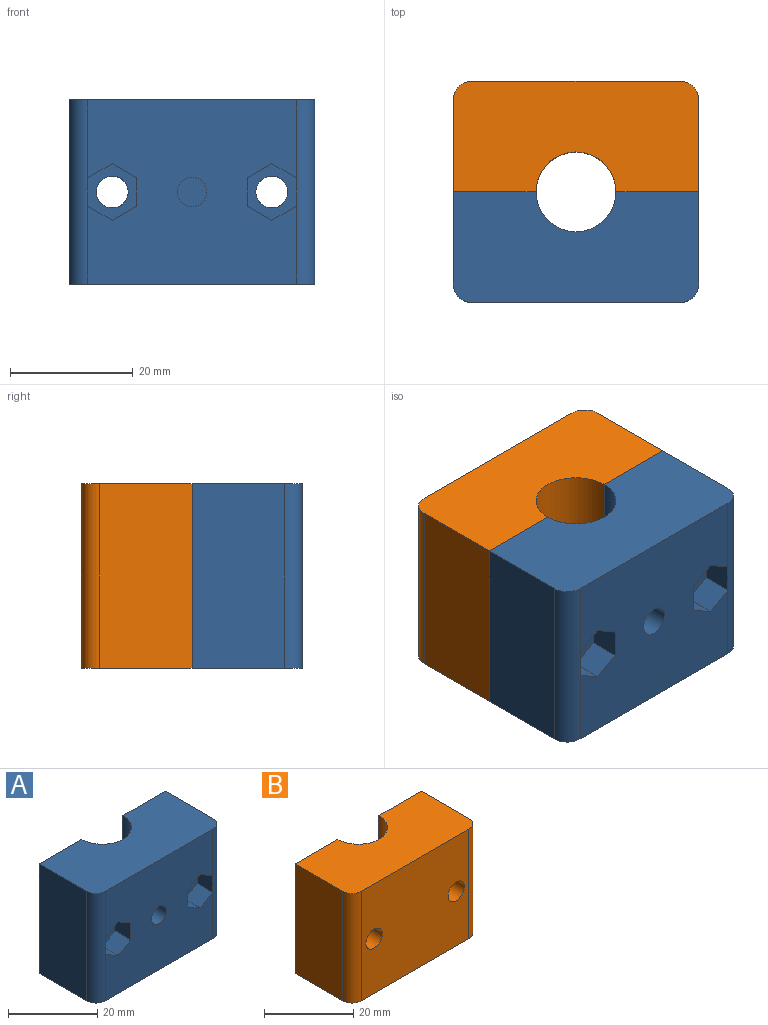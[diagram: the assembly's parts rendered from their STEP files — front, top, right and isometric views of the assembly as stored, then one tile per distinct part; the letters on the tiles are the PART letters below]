
ASSEMBLY  parts=2 mates=1
PART A: 28 faces, bbox 40x18x30 mm
  f0: plane 34x30mm, normal (0,-1,0), area 891.1mm2, adj f5,f6,f10,f11,f12,f14,f15,f17
  f1: cylinder r=2.6mm len=13mm, axis (0,-1,0), area 212.4mm2, adj f8,f27
  f2: cylinder r=2.6mm len=13mm, axis (0,-1,0), area 212.4mm2, adj f3,f20
  f3: plane 30x13.5mm, normal (0,1,0), area 383.8mm2, adj f2,f4,f9,f10,f11
  f4: plane 30x15mm, normal (-1,0,0), area 450mm2, adj f3,f5,f10,f11
  f5: cylinder r=3mm len=30mm, axis (0,0,-1), area 141.4mm2, adj f0,f4,f10,f11,f16
  f6: cylinder r=3mm len=30mm, axis (0,0,-1), area 141.4mm2, adj f0,f7,f10,f11,f26
  f7: plane 30x15mm, normal (1,0,0), area 450mm2, adj f6,f8,f10,f11
  f8: plane 30x13.5mm, normal (0,1,0), area 383.8mm2, adj f1,f7,f9,f10,f11
  f9: cylinder r=6.5mm len=30mm, axis (0,0,-1), area 612.6mm2, adj f3,f8,f10,f11
  f10: plane 40x18mm, normal (0,0,1), area 649.8mm2, adj f0,f3,f4,f5,f6,f7,f8,f9
  f11: plane 40x18mm, normal (0,0,-1), area 649.8mm2, adj f0,f3,f4,f5,f6,f7,f8,f9
  f12: cylinder r=2.4mm len=9mm, axis (0,-1,0), area 135.7mm2, adj f0,f13
  f13: plane 4.8x4.8mm, normal (0,-1,0), area 18.1mm2, adj f12
  f14: plane 5x4mm, normal (-0.5,0,-0.87), area 23.1mm2, adj f0,f15,f19,f20
  f15: plane 5x4mm, normal (0.5,0,-0.87), area 23.1mm2, adj f0,f14,f16,f20
  f16: plane 5x4.62mm, normal (1,0,0), area 23.1mm2, adj f5,f15,f17,f20
  f17: plane 5x4mm, normal (0.5,0,0.87), area 23.1mm2, adj f0,f16,f18,f20
  f18: plane 5x4mm, normal (-0.5,0,0.87), area 23.1mm2, adj f0,f17,f19,f20
  f19: plane 5x4.62mm, normal (-1,0,0), area 23.1mm2, adj f0,f14,f18,f20
  f20: plane 9.24x8mm, normal (0,-1,0), area 34.2mm2, adj f2,f14,f15,f16,f17,f18,f19
  f21: plane 5x4mm, normal (-0.5,0,-0.87), area 23.1mm2, adj f0,f22,f26,f27
  f22: plane 5x4mm, normal (0.5,0,-0.87), area 23.1mm2, adj f0,f21,f23,f27
  f23: plane 5x4.62mm, normal (1,0,0), area 23.1mm2, adj f0,f22,f24,f27
  f24: plane 5x4mm, normal (0.5,0,0.87), area 23.1mm2, adj f0,f23,f25,f27
  f25: plane 5x4mm, normal (-0.5,0,0.87), area 23.1mm2, adj f0,f24,f26,f27
  f26: plane 5x4.62mm, normal (-1,0,0), area 23.1mm2, adj f6,f21,f25,f27
  f27: plane 9.24x8mm, normal (0,-1,0), area 34.2mm2, adj f1,f21,f22,f23,f24,f25,f26
PART B: 12 faces, bbox 40x18x30 mm
  f0: plane 34x30mm, normal (0,-1,0), area 977.5mm2, adj f3,f4,f8,f9,f10,f11
  f1: plane 30x13.5mm, normal (0,1,0), area 383.8mm2, adj f2,f7,f8,f9,f11
  f2: plane 30x15mm, normal (-1,0,0), area 450mm2, adj f1,f3,f8,f9
  f3: cylinder r=3mm len=30mm, axis (0,0,-1), area 141.4mm2, adj f0,f2,f8,f9
  f4: cylinder r=3mm len=30mm, axis (0,0,-1), area 141.4mm2, adj f0,f5,f8,f9
  f5: plane 30x15mm, normal (1,0,0), area 450mm2, adj f4,f6,f8,f9
  f6: plane 30x13.5mm, normal (0,1,0), area 383.8mm2, adj f5,f7,f8,f9,f10
  f7: cylinder r=6.5mm len=30mm, axis (0,0,-1), area 612.6mm2, adj f1,f6,f8,f9
  f8: plane 40x18mm, normal (0,0,1), area 649.8mm2, adj f0,f1,f2,f3,f4,f5,f6,f7
  f9: plane 40x18mm, normal (0,0,-1), area 649.8mm2, adj f0,f1,f2,f3,f4,f5,f6,f7
  f10: cylinder r=2.6mm len=18mm, axis (0,-1,0), area 294.1mm2, adj f0,f6
  f11: cylinder r=2.6mm len=18mm, axis (0,-1,0), area 294.1mm2, adj f0,f1
PLACE A t=(-17.52,2.9,-8.98)mm fixed
PLACE B rot(axis=(0,0,1),180deg) t=(-17.52,2.9,-8.98)mm
MATE slider A.f2 <-> B.f10  axis (0,1,0) through (-30.52,2.9,6.02)mm
